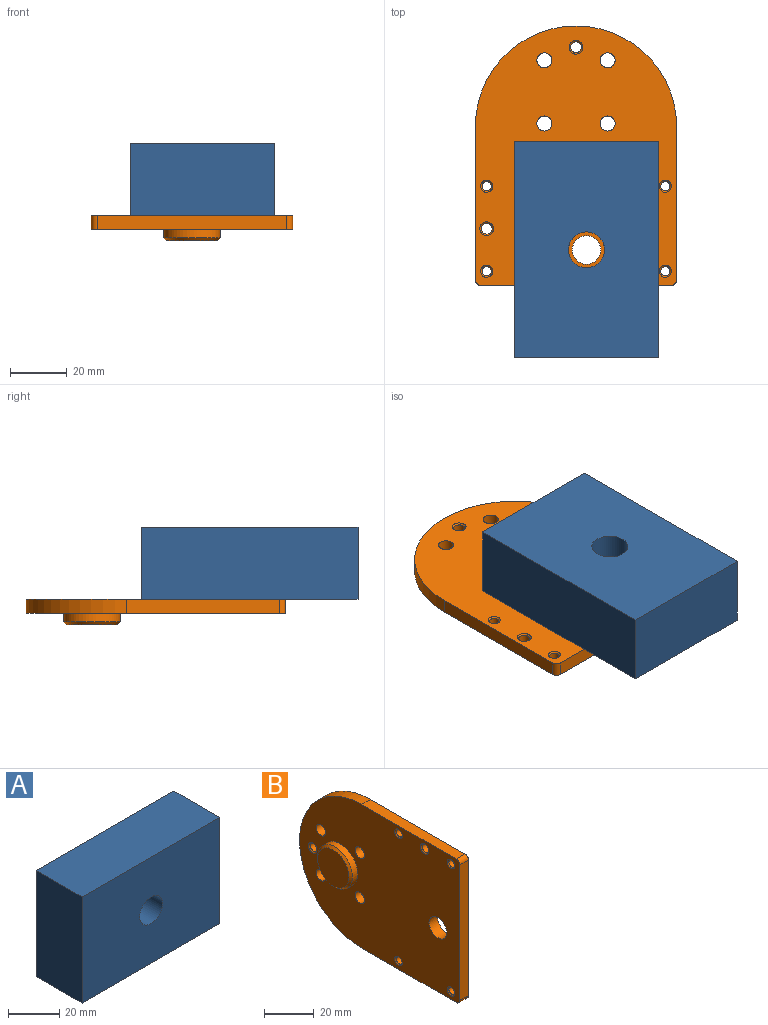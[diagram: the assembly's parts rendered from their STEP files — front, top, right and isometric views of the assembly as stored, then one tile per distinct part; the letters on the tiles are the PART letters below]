
ASSEMBLY  parts=2 mates=1
PART A: 7 faces, bbox 76.2x25.4x50.8 mm
  f0: plane 76.2x50.8mm, normal (0,-1,0), area 3744.3mm2, adj f2,f3,f4,f5,f6
  f1: plane 76.2x50.8mm, normal (0,1,0), area 3744.3mm2, adj f2,f3,f4,f5,f6
  f2: plane 50.8x25.4mm, normal (1,0,0), area 1290.3mm2, adj f0,f1,f3,f5
  f3: plane 76.2x25.4mm, normal (0,0,1), area 1935.5mm2, adj f0,f1,f2,f4
  f4: plane 50.8x25.4mm, normal (-1,0,0), area 1290.3mm2, adj f0,f1,f3,f5
  f5: plane 76.2x25.4mm, normal (0,0,-1), area 1935.5mm2, adj f0,f1,f2,f4
  f6: cylinder r=6.35mm len=25.4mm, axis (0,1,0), area 1013.4mm2, adj f0,f1
PART B: 34 faces, bbox 9x91.5x71 mm
  f0: cylinder r=9.95mm len=19.9mm, axis (-1,0,0), area 187.6mm2, adj f6,f22
  f1: plane 17.9x17.9mm, normal (-1,0,0), area 251.6mm2, adj f22
  f2: plane 67x5mm, normal (0,-1,0), area 335mm2, adj f5,f6,f23,f24
  f3: plane 53.99x5mm, normal (0,0,-1), area 269.9mm2, adj f5,f6,f23,f25
  f4: plane 53.99x5mm, normal (0,0,1), area 269.9mm2, adj f5,f6,f24,f25
  f5: plane 91.49x71mm, normal (1,0,0), area 5689.8mm2, adj f2,f3,f4,f8,f9,f10,f11,f21
  f6: plane 91.49x71mm, normal (-1,0,0), area 5378.8mm2, adj f0,f2,f3,f4,f8,f9,f10,f11
  f7: cylinder r=1.93mm len=4mm, axis (-1,0,0), area 48.4mm2, adj f20,f21
  f8: cylinder r=2.65mm len=5.3mm, axis (-1,0,0), area 83.3mm2, adj f5,f6
  f9: cylinder r=2.65mm len=5.3mm, axis (-1,0,0), area 83.3mm2, adj f5,f6
  f10: cylinder r=2.65mm len=5.3mm, axis (-1,0,0), area 83.3mm2, adj f5,f6
  f11: cylinder r=2.65mm len=5.3mm, axis (-1,0,0), area 83.3mm2, adj f5,f6
  f12: cylinder r=1.65mm len=4mm, axis (1,0,0), area 41.5mm2, adj f19,f29
  f13: cylinder r=1.65mm len=4mm, axis (1,0,0), area 41.5mm2, adj f18,f30
  f14: cylinder r=1.65mm len=4mm, axis (1,0,0), area 41.5mm2, adj f17,f31
  f15: cylinder r=1.65mm len=4mm, axis (1,0,0), area 41.5mm2, adj f16,f28
  f16: cone r=1.65mm half-angle=45deg, axis (-1,0,0), area 8.4mm2, adj f6,f15
  f17: cone r=1.65mm half-angle=45deg, axis (-1,0,0), area 8.4mm2, adj f6,f14
  f18: cone r=1.65mm half-angle=45deg, axis (-1,0,0), area 8.4mm2, adj f6,f13
  f19: cone r=1.65mm half-angle=45deg, axis (-1,0,0), area 8.4mm2, adj f6,f12
  f20: cone r=2.43mm half-angle=45deg, axis (-1,0,0), area 9.7mm2, adj f6,f7
  f21: cone r=2.43mm half-angle=45deg, axis (1,0,0), area 9.7mm2, adj f5,f7
  f22: cone r=9.95mm half-angle=45deg, axis (1,0,0), area 84mm2, adj f0,f1
  f23: cylinder r=2mm len=5mm, axis (-1,0,0), area 15.7mm2, adj f2,f3,f5,f6
  f24: cylinder r=2mm len=5mm, axis (1,0,0), area 15.7mm2, adj f2,f4,f5,f6
  f25: cylinder r=35.5mm len=71mm, axis (-1,0,0), area 557.6mm2, adj f3,f4,f5,f6
  f26: cylinder r=1.93mm len=4mm, axis (1,0,0), area 48.4mm2, adj f32,f33
  f27: cylinder r=5.04mm len=10.08mm, axis (1,0,0), area 158.4mm2, adj f5,f6
  f28: cone r=1.65mm half-angle=45deg, axis (1,0,0), area 8.4mm2, adj f5,f15
  f29: cone r=1.65mm half-angle=45deg, axis (1,0,0), area 8.4mm2, adj f5,f12
  f30: cone r=1.65mm half-angle=45deg, axis (1,0,0), area 8.4mm2, adj f5,f13
  f31: cone r=1.65mm half-angle=45deg, axis (1,0,0), area 8.4mm2, adj f5,f14
  f32: cone r=1.93mm half-angle=45deg, axis (-1,0,0), area 9.7mm2, adj f6,f26
  f33: cone r=1.93mm half-angle=45deg, axis (1,0,0), area 9.7mm2, adj f5,f26
PLACE A rot(axis=(0.58,-0.58,-0.58),120deg) t=(357.25,-55.74,664.45)mm
PLACE B rot(axis=(0,-1,0),90deg) t=(983.55,0,272.75)mm
MATE pin_slot A.f6 <-> B.f5  axis (0,0,-1) through (357.25,-55.74,651.75)mm
